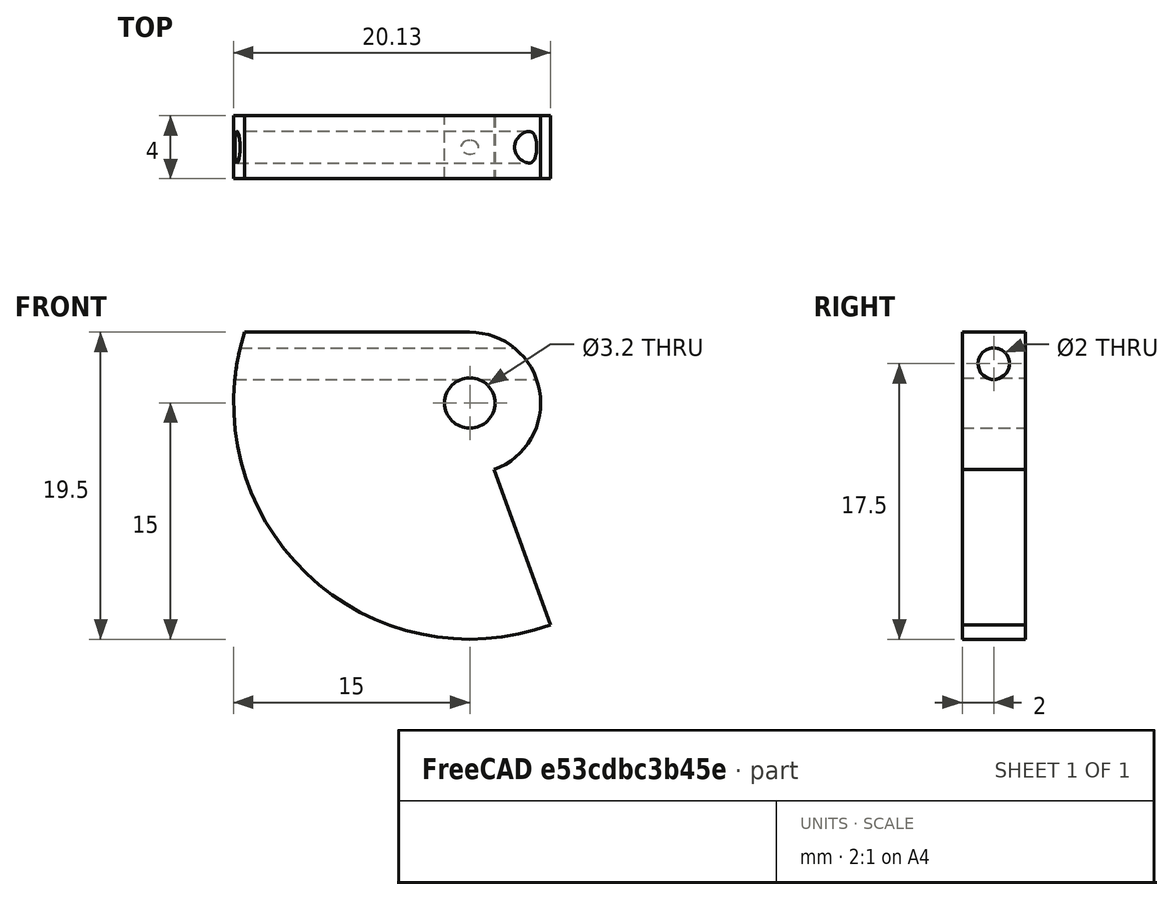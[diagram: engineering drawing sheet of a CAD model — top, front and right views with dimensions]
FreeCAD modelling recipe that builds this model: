
FCSTD DOCUMENT  (FreeCAD 0.19R24291 (Git))
Label: OptoEndStopFlag_v3
License: All rights reserved
LicenseURL: http://en.wikipedia.org/wiki/All_rights_reserved
objects: Sketcher::SketchObject×2, PartDesign::Pad×1, PartDesign::Pocket×1, PartDesign::Body×1, App::Part×1, Mesh::Feature×1
note: 7 computed .brp shape members not serialized (recipe doc carries the construction recipe); baked Part::Feature solids carry a one-line shape summary decoded from their .brp

FEATURE [Sketcher::SketchObject] Sketch006
  FullyConstrained = false
  MapMode = 5
  Placement = pos=(0,0,0) rot=(1,0,0;1.5708rad)
  Support = -> [XZ_Plane002]
  sketch-geometry (6):
    g0: Circle CenterX=0 CenterY=0 CenterZ=0 NormalX=0 NormalY=0 NormalZ=1 AngleXU=0 Radius=1.6
    g1: ArcOfCircle CenterX=0 CenterY=0 CenterZ=0 NormalX=0 NormalY=0 NormalZ=1 AngleXU=0 Radius=15 StartAngle=2.8369 EndAngle=5.06145
    g2: ArcOfCircle CenterX=0 CenterY=0 CenterZ=0 NormalX=0 NormalY=0 NormalZ=1 AngleXU=0 Radius=4.5 StartAngle=5.06145 EndAngle=7.85677
    g3: LineSegment StartX=-14.3091 StartY=4.49998 StartZ=0 EndX=-0.0125561 EndY=4.49998 EndZ=0
    g4: LineSegment StartX=5.1303 StartY=-14.0954 StartZ=0 EndX=1.53909 EndY=-4.22862 EndZ=0
    g5: LineSegment StartX=0 StartY=0 StartZ=0 EndX=5.25995 EndY=-14.4516 EndZ=0
  constraints (15):
    c: Coincident(g0,g-1)
    c: Coincident(g1,g0)
    c: Coincident(g2,g0)
    c: Coincident(g3,g1)
    c: Coincident(g3,g2)
    c: Coincident(g4,g1)
    c: Coincident(g4,g2)
    c: Horizontal(g3)
    c: Diameter(g0) = 3.2
    c: Diameter(g2) = 9
    c: Diameter(g1) = 30
    c: Coincident(g5,g0)
    c: PointOnObject(g2,g5)
    c: PointOnObject(g1,g5)
    c: Angle(g5,g-1) = 1.22173
FEATURE [PartDesign::Pad] Pad001
  Direction = (1,1,1)
  Length = 4
  Length2 = 100
  Placement = pos=(0,0,0) rot=(1,0,0;1.5708rad)
  Profile = -> Sketch006
  Type = 0
FEATURE [Sketcher::SketchObject] Sketch007
  FullyConstrained = true
  MapMode = 5
  Placement = pos=(0,0,0) rot=(0.57735,0.57735,0.57735;2.0944rad)
  Support = -> [YZ_Plane002]
  sketch-geometry (1):
    g0: Circle CenterX=-2 CenterY=2.5 CenterZ=0 NormalX=0 NormalY=0 NormalZ=1 AngleXU=0 Radius=1
  constraints (3):
    c: DistanceX(g-2,g0) = -2
    c: DistanceY(g-1,g0) = 2.5
    c: Diameter(g0) = 2
FEATURE [PartDesign::Pocket] Pocket
  BaseFeature = -> Pad001
  Length = 5
  Length2 = 100
  Midplane = true
  Placement = pos=(0,0,0) rot=(1,0,0;1.5708rad)
  Profile = -> Sketch007
  Type = 1
FEATURE [PartDesign::Body] Body001  label="bFlag"
  Group = -> [Sketch006,Pad001,Sketch007,Pocket]
  Origin = -> Origin002
  Tip = -> Pocket
FEATURE [App::Part] Part  label="pFlag"
  Group = -> [Body001]
  Origin = -> Origin
FEATURE [Mesh::Feature] Mesh  label="Pocket (Meshed)"
